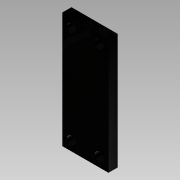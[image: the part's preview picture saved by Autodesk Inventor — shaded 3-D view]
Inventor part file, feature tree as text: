
AUTODESK INVENTOR PART (.ipt)
format: ipt  version: 2015 SP1 (Build 190203100, 203)  size: 101,888 bytes
history: native  units: mm
features: extrude x1, sketch x1
ambient origin geometry x8: Origin, YZ Plane, XZ Plane, XY Plane, X Axis, Y Axis, Z Axis, Center Point
bodies: Solid1 (feature_tree)
feature tree (2):
  extrude  "Extrusion1"  Depth=10.0mm
  sketch  "Sketch1"  dims[d0=25.0mm d1=10.0mm d3=2.0mm d4=2.0mm d5=2.0mm d6=2.0mm d7=2.0mm d8=2.0mm d9=2.0mm d10=2.0mm d11=2.0mm d12=0.0mm d13=2.0mm d14=2.0mm d15=2.0mm d16=2.0mm]
